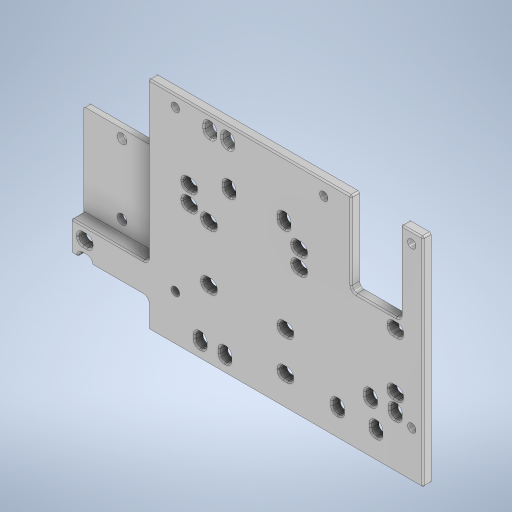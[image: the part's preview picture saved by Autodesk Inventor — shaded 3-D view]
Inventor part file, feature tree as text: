
AUTODESK INVENTOR PART (.ipt)
format: ipt  version: 2024 (Build 280153000, 153)  size: 1,369,088 bytes
history: native  units: mm
features: extrude x16, fillet x11, sketch x10, projected_geometry x5, chamfer x1
ambient origin geometry x8: Origin, YZ Plane, XZ Plane, XY Plane, X Axis, Y Axis, Z Axis, Center Point
bodies: Solid1 (feature_tree)
feature tree (43):
  extrude  "Extrusion1"  Depth=79.0mm
  extrude  "Extrusion2"  Depth=3.0mm
  fillet  "Fillet1"  Radius=3.0mm
  extrude  "Extrusion3"  Depth=4.0mm
  extrude  "Extrusion4"  Depth=4.0mm
  extrude  "Extrusion5"  Depth=2.0mm TaperAngle=0.0deg
  extrude  "Extrusion6"  Depth=4.0mm
  fillet  "Fillet2"  Radius=4.0mm
  fillet  "Fillet3"  Radius=4.0mm
  fillet  "Fillet4"  Radius=4.0mm
  extrude  "Extrusion7"  Depth=4.0mm
  extrude  "Extrusion8"  Depth=4.0mm
  fillet  "Fillet5"  Radius=4.0mm
  extrude  "Extrusion9"  Depth=5.0mm
  fillet  "Fillet6"  Radius=5.0mm
  sketch  "Sketch11"  dims[d10=33.0mm d11=2.0mm d12=0.0mm]
  extrude  "Extrusion10"  Depth=5.0mm
  extrude  "Extrusion11"  Depth=5.0mm
  extrude  "Extrusion12"  Depth=5.0mm
  fillet  "Fillet7"  Radius=5.0mm
  extrude  "Extrusion13"  Depth=5.0mm
  extrude  "Extrusion14"  TaperAngle=0.0deg  [1 undecoded]
  fillet  "Fillet8"  Radius=20.0mm
  fillet  "Fillet9"  Radius=20.0mm
  extrude  "Extrusion15"  Depth=14.0mm
  fillet  "Fillet10"  Radius=14.0mm
  extrude  "Extrusion16"  Depth=17.0mm
  fillet  "Fillet11"  Radius=10.0mm
  chamfer  "Chamfer1"  Distance=25.0mm
  sketch  "Sketch2"  dims[d0=100.0mm d1=79.0mm]
  sketch  "Sketch3"  dims[d2=3.0mm d3=0.0mm d4=3.0mm d5=3.0mm]
  projected_geometry  "Projected Loop1"
  sketch  "Sketch9"  dims[d6=86.0mm d7=4.0mm]
  projected_geometry  "Projected Loop2"
  sketch  "Sketch10"  dims[d8=4.0mm d9=4.0mm]
  projected_geometry  "Projected Loop3"
  sketch  "Sketch12"  dims[d13=0.6mm d14=4.0mm d15=4.0mm d16=4.0mm d17=4.0mm]
  projected_geometry  "Projected Loop4"
  sketch  "Sketch13"  dims[d18=4.0mm d19=4.0mm]
  projected_geometry  "Projected Loop5"
  sketch  "Sketch14"  dims[d20=4.0mm d21=4.0mm d23=4.0mm]
  sketch  "Sketch15"  dims[d24=5.0mm d25=5.0mm d26=5.0mm]
  sketch  "Sketch16"  dims[d27=5.0mm d29=5.0mm d30=5.0mm d31=5.0mm d32=5.0mm d33=5.0mm d34=0.0mm d35=20.0mm d36=20.0mm d37=14.0mm d38=14.0mm d40=17.0mm d41=10.0mm d42=25.0mm d43=50.0mm d44=34.0mm d45=4.0mm d46=5.0mm d47=20.0mm d48=0.0mm d49=0.0mm d50=10.0mm d51=0.0mm d52=0.0mm d54=4.0mm d55=5.0mm d56=4.0mm d57=5.0mm d60=4.0mm d61=5.0mm d62=2.0mm d63=5.0mm d64=0.0mm d65=5.0mm d66=19.0mm d67=6.0mm d72=4.0mm d73=5.0mm d74=4.0mm d75=5.0mm d76=0.0mm d77=5.0mm d78=2.0mm d79=5.0mm d80=2.0mm d81=5.0mm d82=10.022273mm d83=2.022273mm d84=4.0mm d85=0.0mm d86=0.0mm d87=5.0mm d88=4.0mm d89=4.0mm d90=4.0mm d91=5.0mm d92=5.0mm d93=6.0mm d98=3.5mm d102=26.0mm d103=15.0mm d105=4.0mm d106=4.0mm d107=5.0mm d108=5.0mm d109=6.0mm d116=2.0mm d117=5.0mm d121=0.0mm d122=45.0mm d123=0.0mm d124=0.0mm d125=20.0mm d126=29.5mm d127=30.0mm d128=8.0mm d129=18.0mm d130=0.0mm d131=0.0mm d132=0.6mm d133=1.75mm d134=1.75mm d135=1.75mm d136=3.0mm d137=5.0mm d138=10.0mm d139=10.0mm d140=0.0mm d141=0.5mm d142=2.0mm d143=45.0deg d145=8.0mm d146=12.2mm d147=41.0mm d148=1.5mm d149=0.0mm d151=28.5mm d152=1.75mm d153=21.0mm d154=33.0mm d155=2.25mm d156=0.0mm d157=1.75mm d158=54.0mm d159=3.0mm d160=28.0mm d161=2.25mm d162=0.0mm d163=33.0mm d164=3.6mm d165=0.0mm d166=4.6mm d167=0.0mm d168=1.75mm d169=3.5mm d170=3.5mm d171=25.4mm d172=3.175mm d173=0.0mm d174=0.0mm d175=10.0mm d176=0.0mm d177=0.0mm d178=1.75mm d179=0.6mm d180=2.0mm d181=10.0mm d182=0.0mm d183=0.6mm d187=1.75mm d188=1.5mm d189=0.5mm d190=5.0mm d193=10.0mm d194=0.0mm d195=0.6mm d196=2.5mm d197=2.5mm d198=1.75mm d199=0.5mm d200=0.5mm d201=1.5mm d202=1.5mm d203=22.5mm d204=5.0mm]
note: 1 required parameter value undecoded (feature->parameter linkage not recoverable at this tier; creation-order binding heuristic only, values carry confidence <= 0.55)
